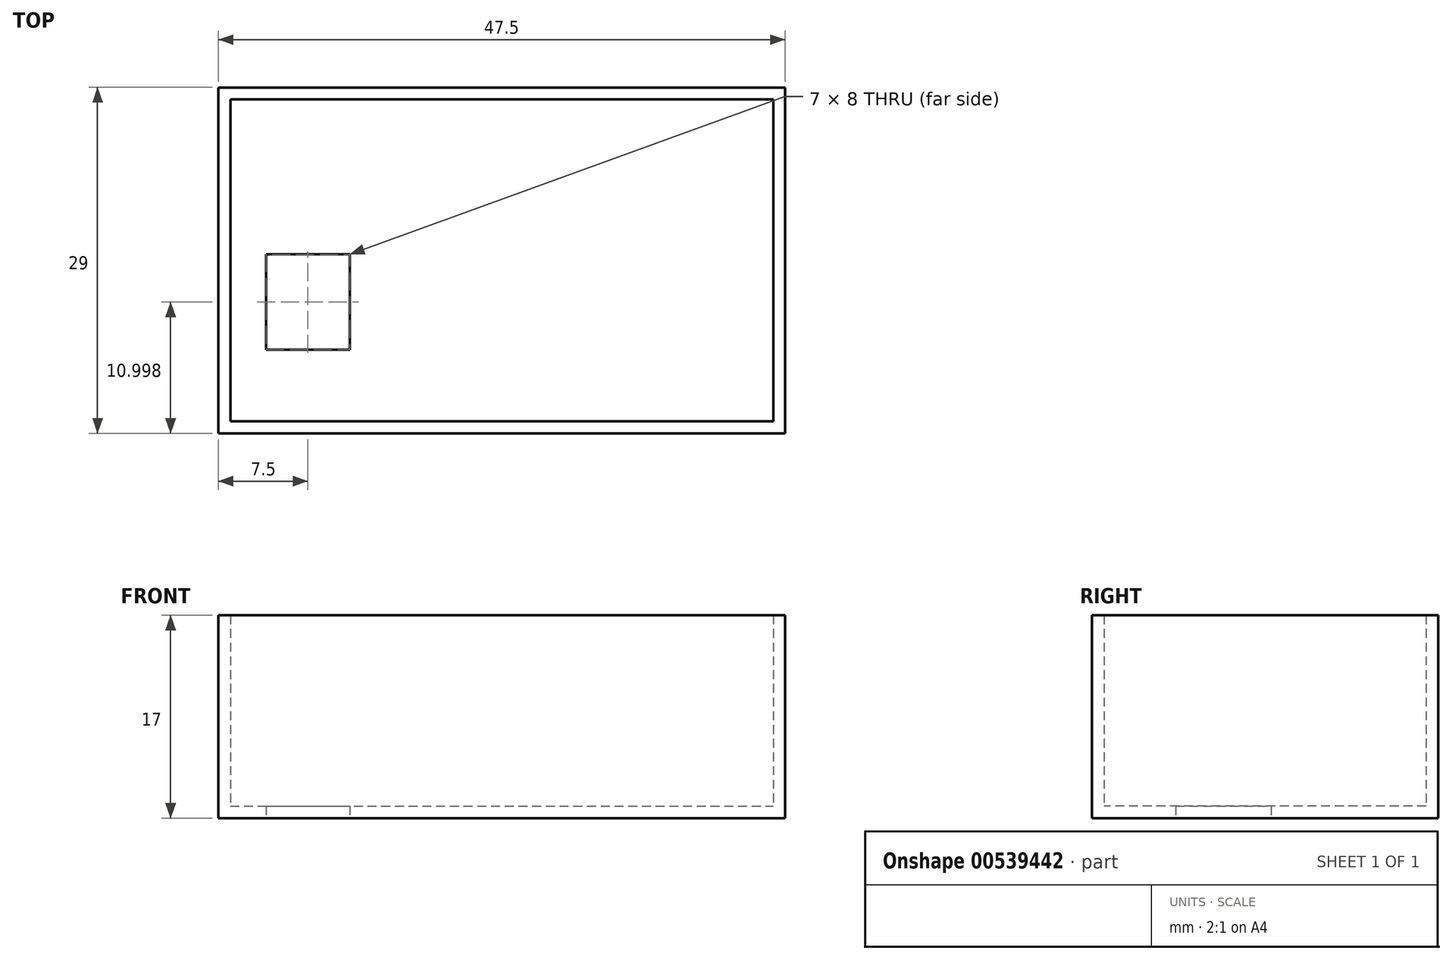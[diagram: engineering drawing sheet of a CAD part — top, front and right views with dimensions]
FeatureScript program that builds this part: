
annotation { "Feature Type Name" : "Feature", "Feature Type Description" : "" }
export const myFeature = defineFeature(function(context is Context, id is Id, definition is map)
    precondition{}
    {
        {
            var Q0;
            Q0=qCreatedBy(makeId("Top.planeOp"),FACE);
            var sketch = newSketch(context, id + "F0", { "sketchPlane" : qUnion([Q0])});
            skLineSegment(sketch, "E0.bottom", {"start": v(-24.82, 13.7) * mm, "end": v(20.68, 13.7) * mm});
            skLineSegment(sketch, "E0.top", {"start": v(-24.82, -13.3) * mm, "end": v(20.68, -13.3) * mm});
            skLineSegment(sketch, "E0.left", {"start": v(-24.82, 13.7) * mm, "end": v(-24.82, -13.3) * mm});
            skLineSegment(sketch, "E0.right", {"start": v(20.68, 13.7) * mm, "end": v(20.68, -13.3) * mm});
            skLineSegment(sketch, "E1.0", {"start": v(-25.82, 14.7) * mm, "end": v(21.68, 14.7) * mm});
            skLineSegment(sketch, "E1.1", {"start": v(-25.82, 14.7) * mm, "end": v(-25.82, -14.3) * mm});
            skLineSegment(sketch, "E1.2", {"start": v(-25.82, -14.3) * mm, "end": v(21.68, -14.3) * mm});
            skLineSegment(sketch, "E1.3", {"start": v(21.68, 14.7) * mm, "end": v(21.68, -14.3) * mm});
            skSolve(sketch);
        }
        {
            var Q0;
            Q0=makeQuery(id+"F0.imprint","IMPRINT",FACE,{"disambiguationData":[TD([[makeQuery(id+"F0.imprint","IMPRINT",EDGE,{"derivedFrom":sQuery(id+"F0.wireOp",EDGE,"E0.bottom")}),-1.0]])]});
            extrude(context, id + "F1", {"entities" : qUnion([Q0]), "depth" : 1 * mm, "offsetDistance" : 25 * mm});
        }
        {
            var Q0;
            Q0=makeQuery(id+"F0.imprint","IMPRINT",FACE,{"disambiguationData":[TD([[makeQuery(id+"F0.imprint","IMPRINT",EDGE,{"derivedFrom":sQuery(id+"F0.wireOp",EDGE,"E0.bottom")}),1.0]])]});
            extrude(context, id + "F2", {"entities" : qUnion([Q0]), "operationType" : NewBodyOperationType.ADD, "depth" : 17 * mm, "offsetDistance" : 25 * mm});
        }
        {
            var Q0;
            Q0=makeQuery(id+"F0.imprint","IMPRINT",FACE,{"disambiguationData":[TD([[makeQuery(id+"F0.imprint","IMPRINT",EDGE,{"derivedFrom":sQuery(id+"F0.wireOp",EDGE,"E0.bottom")}),-1.0]])]});
            var sketch = newSketch(context, id + "F3", { "sketchPlane" : qUnion([Q0])});
            skLineSegment(sketch, "E2.bottom", {"start": v(-14.82, 0.7) * mm, "end": v(-21.82, 0.7) * mm});
            skLineSegment(sketch, "E2.top", {"start": v(-14.82, -7.3) * mm, "end": v(-21.82, -7.3) * mm});
            skLineSegment(sketch, "E2.left", {"start": v(-14.82, 0.7) * mm, "end": v(-14.82, -7.3) * mm});
            skLineSegment(sketch, "E2.right", {"start": v(-21.82, 0.7) * mm, "end": v(-21.82, -7.3) * mm});
            skSolve(sketch);
        }
        {
            var Q0;
            Q0 = qSketchRegion(id + "F3", true);
            extrude(context, id + "F4", {"entities" : qUnion([Q0]), "operationType" : NewBodyOperationType.REMOVE, "endBound" : BoundingType.THROUGH_ALL, "depth" : 25 * mm, "offsetDistance" : 25 * mm});
        }
    });
